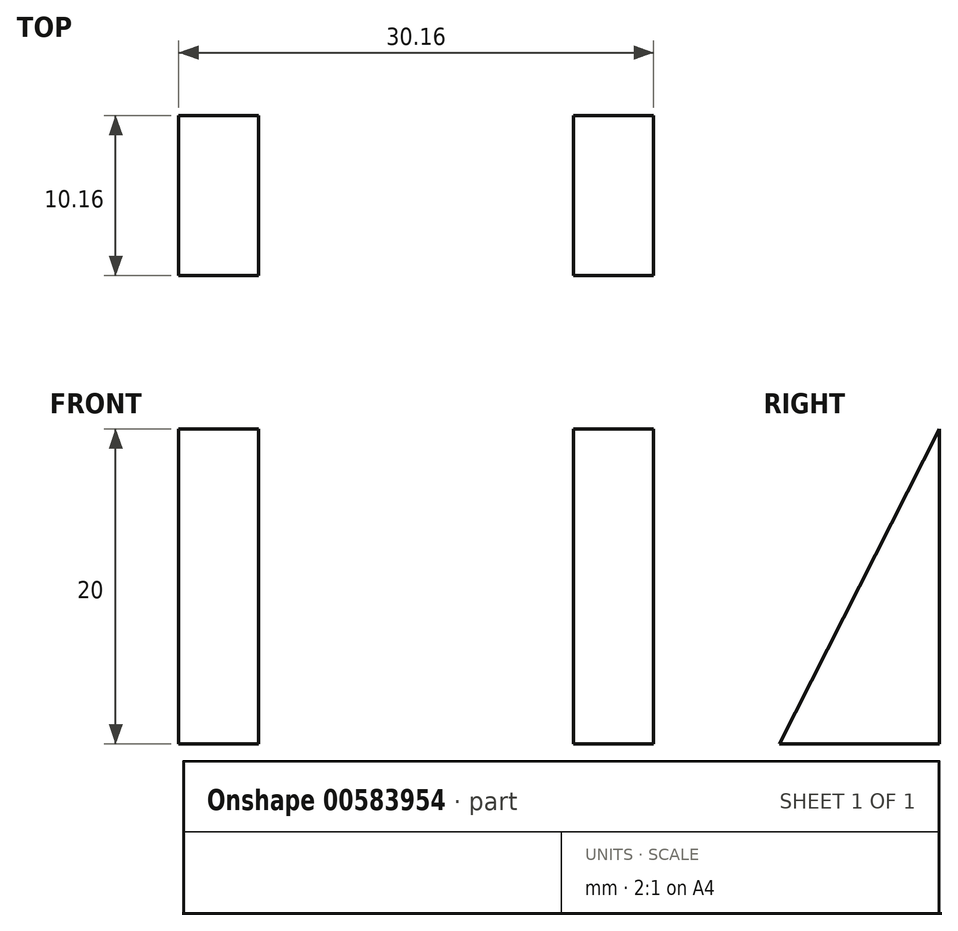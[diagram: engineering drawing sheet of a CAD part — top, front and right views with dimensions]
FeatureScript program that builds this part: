
annotation { "Feature Type Name" : "Feature", "Feature Type Description" : "" }
export const myFeature = defineFeature(function(context is Context, id is Id, definition is map)
    precondition{}
    {
        {
            var Q0;
            Q0=qCreatedBy(makeId("Right.planeOp"),FACE);
            var sketch = newSketch(context, id + "F0", { "sketchPlane" : qUnion([Q0])});
            skLineSegment(sketch, "E0", {"start": v(0, 0) * mm, "end": v(-10.16, 0) * mm});
            skLineSegment(sketch, "E1", {"start": v(0, 0) * mm, "end": v(0, 20) * mm});
            skLineSegment(sketch, "E2", {"start": v(0, 20) * mm, "end": v(-10.16, 0) * mm});
            skSolve(sketch);
        }
        {
            var Q0;
            Q0=makeQuery(id+"F0.imprint","IMPRINT",FACE,{"disambiguationData":[TD([[makeQuery(id+"F0.imprint","IMPRINT",EDGE,{"derivedFrom":sQuery(id+"F0.wireOp",EDGE,"E0")}),-1.0]])]});
            extrude(context, id + "F1", {"entities" : qUnion([Q0]), "depth" : 30.16 * mm, "offsetDistance" : 25.4 * mm});
        }
        {
            var Q0;
            Q0=makeQuery(id+"F1.opExtrude","SWEPT_FACE",FACE,{"disambiguationData":[OSD([sQuery(id+"F0.wireOp",EDGE,"E1")])]});
            var sketch = newSketch(context, id + "F2", { "sketchPlane" : qUnion([Q0])});
            skLineSegment(sketch, "E3.bottom", {"start": v(-30.16, 0) * mm, "end": v(-25.08, 0) * mm});
            skLineSegment(sketch, "E3.top", {"start": v(-30.16, 20) * mm, "end": v(-25.08, 20) * mm});
            skLineSegment(sketch, "E3.left", {"start": v(-30.16, 0) * mm, "end": v(-30.16, 20) * mm});
            skLineSegment(sketch, "E3.right", {"start": v(-25.08, 0) * mm, "end": v(-25.08, 20) * mm});
            skLineSegment(sketch, "E4.bottom", {"start": v(0, 0) * mm, "end": v(-5.08, 0) * mm});
            skLineSegment(sketch, "E4.top", {"start": v(0, 20) * mm, "end": v(-5.08, 20) * mm});
            skLineSegment(sketch, "E4.left", {"start": v(0, 0) * mm, "end": v(0, 20) * mm});
            skLineSegment(sketch, "E4.right", {"start": v(-5.08, 0) * mm, "end": v(-5.08, 20) * mm});
            skSolve(sketch);
        }
        {
            var Q0;
            {var subQ0=sQuery(id+"F2.wireOp",EDGE,"E3.right");Q0=makeQuery(id+"F2.imprint","IMPRINT",FACE,{"disambiguationData":[TD([[makeQuery(id+"F2.imprint","IMPRINT",EDGE,{"derivedFrom":subQ0}),-1.0]])]});}
            extrude(context, id + "F3", {"entities" : qUnion([Q0]), "operationType" : NewBodyOperationType.REMOVE, "endBound" : BoundingType.THROUGH_ALL, "oppositeDirection" : true, "depth" : 25.4 * mm, "offsetDistance" : 25.4 * mm});
        }
    });
